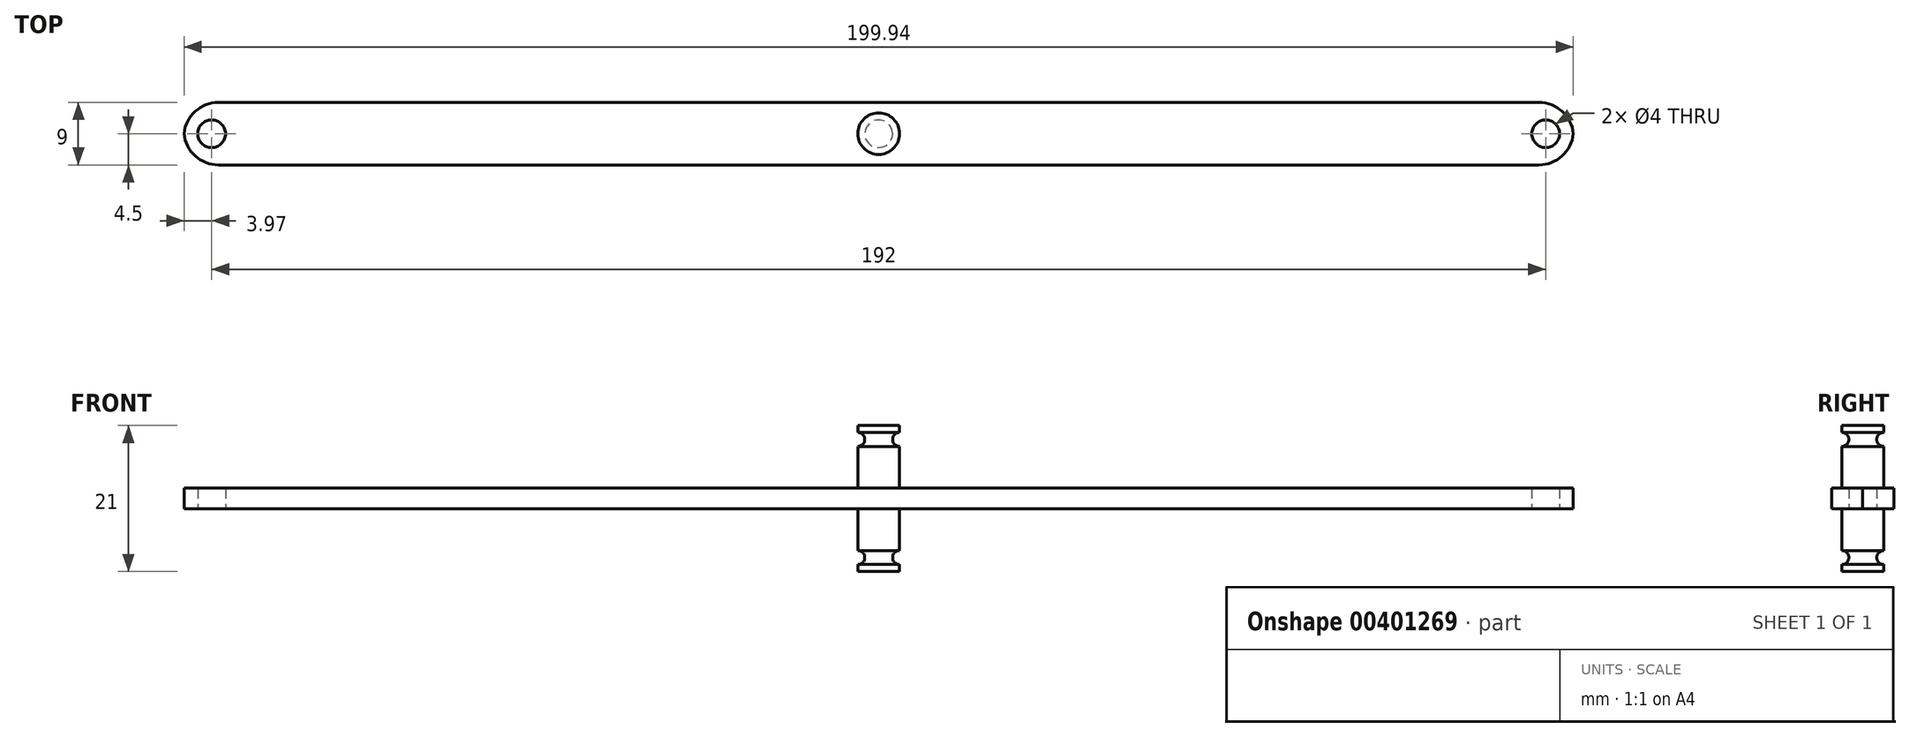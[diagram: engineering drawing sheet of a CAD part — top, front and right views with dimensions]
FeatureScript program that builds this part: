
annotation { "Feature Type Name" : "Feature", "Feature Type Description" : "" }
export const myFeature = defineFeature(function(context is Context, id is Id, definition is map)
    precondition{}
    {
        {
            var Q0;
            Q0=qCreatedBy(makeId("Top.planeOp"),FACE);
            var sketch = newSketch(context, id + "F0", { "sketchPlane" : qUnion([Q0])});
            skLineSegment(sketch, "E0.bottom", {"start": v(-100, 4.5) * mm, "end": v(100, 4.5) * mm});
            skLineSegment(sketch, "E0.top", {"start": v(-100, -4.5) * mm, "end": v(100, -4.5) * mm});
            skLineSegment(sketch, "E0.left", {"start": v(-100, 4.5) * mm, "end": v(-100, -4.5) * mm});
            skLineSegment(sketch, "E0.right", {"start": v(100, 4.5) * mm, "end": v(100, -4.5) * mm});
            skPoint(sketch, "E0.middle", {"position": v(0, 0) * mm});
            skSolve(sketch);
        }
        {
            var Q0;
            Q0 = qSketchRegion(id + "F0", true);
            extrude(context, id + "F1", {"entities" : qUnion([Q0]), "depth" : 3 * mm});
        }
        {
            var Q0;
            Q0=makeQuery(id+"F1.opExtrude","CAP_FACE",FACE,{"disambiguationData":[OSD([sQuery(id+"F0.wireOp",EDGE,"E0.bottom"),sQuery(id+"F0.wireOp",EDGE,"E0.top"),sQuery(id+"F0.wireOp",EDGE,"E0.left"),sQuery(id+"F0.wireOp",EDGE,"E0.right")])],"isStart":true});
            var sketch = newSketch(context, id + "F2", { "sketchPlane" : qUnion([Q0])});
            skCircle(sketch, "E1", {"center": v(-96, 0) * mm, "radius": 2 * mm});
            skCircle(sketch, "E2.MirrorC", {"center": v(96, 0) * mm, "radius": 2 * mm});
            skSolve(sketch);
        }
        {
            var Q0;
            Q0 = qSketchRegion(id + "F2", true);
            extrude(context, id + "F3", {"entities" : qUnion([Q0]), "operationType" : NewBodyOperationType.REMOVE, "oppositeDirection" : true, "depth" : 25 * mm});
        }
        {
            var Q0;
            Q0=makeQuery(id+"F1.opExtrude","SWEPT_EDGE",EDGE,{"disambiguationData":[OSD([sQuery(id+"F0.wireOp",EDGE,"E0.bottom"),sQuery(id+"F0.wireOp",EDGE,"E0.right")])]});
            var Q1;
            Q1=makeQuery(id+"F1.opExtrude","SWEPT_EDGE",EDGE,{"disambiguationData":[OSD([sQuery(id+"F0.wireOp",EDGE,"E0.top"),sQuery(id+"F0.wireOp",EDGE,"E0.right")])]});
            var Q2;
            Q2=makeQuery(id+"F1.opExtrude","SWEPT_EDGE",EDGE,{"disambiguationData":[OSD([sQuery(id+"F0.wireOp",EDGE,"E0.bottom"),sQuery(id+"F0.wireOp",EDGE,"E0.left")])]});
            var Q3;
            Q3=makeQuery(id+"F1.opExtrude","SWEPT_EDGE",EDGE,{"disambiguationData":[OSD([sQuery(id+"F0.wireOp",EDGE,"E0.top"),sQuery(id+"F0.wireOp",EDGE,"E0.left")])]});
            fillet(context, id + "F4", {"entities" : qUnion([Q0, Q1, Q2, Q3]), "radius" : 5 * mm, "tangentPropagation" : true, "allowEdgeOverflow" : false});
        }
        {
            var Q0;
            Q0=makeQuery(id+"F1.opExtrude","CAP_FACE",FACE,{"disambiguationData":[OSD([sQuery(id+"F0.wireOp",EDGE,"E0.bottom"),sQuery(id+"F0.wireOp",EDGE,"E0.top"),sQuery(id+"F0.wireOp",EDGE,"E0.left"),sQuery(id+"F0.wireOp",EDGE,"E0.right")])],"isStart":false});
            var sketch = newSketch(context, id + "F5", { "sketchPlane" : qUnion([Q0])});
            skCircle(sketch, "E3", {"center": v(0, 0) * mm, "radius": 3 * mm});
            skSolve(sketch);
        }
        {
            var Q0;
            Q0 = qSketchRegion(id + "F5", true);
            extrude(context, id + "F6", {"entities" : qUnion([Q0]), "operationType" : NewBodyOperationType.ADD, "depth" : 9 * mm});
        }
        {
            var Q0;
            Q0=makeQuery(id+"F6.opExtrude","CAP_EDGE",EDGE,{"disambiguationData":[OSD([sQuery(id+"F5.wireOp",EDGE,"E3")])],"isStart":false});
            cPlane(context, id + "F7", {"entities" : qUnion([Q0]), "cplaneType" : CPlaneType.LINE_ANGLE, "offset" : 25 * mm, "angle" : 90 * degree, "width" : 150 * mm, "height" : 150 * mm});
        }
        {
            var Q0;
            Q0=qCreatedBy(id+"F7.planeOp",FACE);
            var sketch = newSketch(context, id + "F8", { "sketchPlane" : qUnion([Q0])});
            skCircle(sketch, "E4", {"center": v(-3, 10) * mm, "radius": 1 * mm});
            skSolve(sketch);
        }
        {
            var Q0;
            Q0=makeQuery(id+"F8.imprint","IMPRINT",FACE,{"disambiguationData":[TD([[makeQuery(id+"F8.imprint","IMPRINT",EDGE,{"derivedFrom":sQuery(id+"F8.wireOp",EDGE,"E4")}),1.0]])]});
            var Q1;
            Q1=sQuery(id+"F8.wireOp",EDGE,"E4");
            var Q2;
            Q2=makeQuery(id+"F6.opExtrude","CAP_EDGE",EDGE,{"disambiguationData":[OSD([sQuery(id+"F5.wireOp",EDGE,"E3")])],"isStart":false});
            revolve(context, id + "F9", {"operationType" : NewBodyOperationType.REMOVE, "entities" : qUnion([Q0]), "surfaceEntities" : qUnion([Q1]), "axis" : qUnion([Q2]), "revolveType" : RevolveType.FULL, "oppositeDirection" : true});
        }
        {
            var Q0;
            {var subQ0=sQuery(id+"F0.wireOp",EDGE,"E0.top");Q0=makeQuery(id+"F4.opFillet","BLEND_EDGE",EDGE,{"blendedFrom":[makeQuery(id+"F1.opExtrude","SWEPT_EDGE",EDGE,{"disambiguationData":[OSD([subQ0,sQuery(id+"F0.wireOp",EDGE,"E0.right")])]}),makeQuery(id+"F1.opExtrude","SWEPT_FACE",FACE,{"disambiguationData":[OSD([subQ0])]})],"blendedInto":[makeQuery(id+"F1.opExtrude","SWEPT_FACE",FACE,{"disambiguationData":[OSD([subQ0])]})]});}
            cPoint(context, id + "F10", {"entities" : qUnion([Q0]), "parameter" : 0.5});
        }
        {
            var Q0;
            {var subQ0=sQuery(id+"F0.wireOp",EDGE,"E0.top");Q0=makeQuery(id+"F4.opFillet","BLEND_EDGE",EDGE,{"blendedFrom":[makeQuery(id+"F1.opExtrude","SWEPT_EDGE",EDGE,{"disambiguationData":[OSD([subQ0,sQuery(id+"F0.wireOp",EDGE,"E0.left")])]}),makeQuery(id+"F1.opExtrude","SWEPT_FACE",FACE,{"disambiguationData":[OSD([subQ0])]})],"blendedInto":[makeQuery(id+"F1.opExtrude","SWEPT_FACE",FACE,{"disambiguationData":[OSD([subQ0])]})]});}
            cPoint(context, id + "F11", {"entities" : qUnion([Q0]), "parameter" : 0.5});
        }
        {
            var Q0;
            {var subQ0=sQuery(id+"F0.wireOp",EDGE,"E0.bottom");Q0=makeQuery(id+"F4.opFillet","BLEND_EDGE",EDGE,{"blendedFrom":[makeQuery(id+"F1.opExtrude","SWEPT_EDGE",EDGE,{"disambiguationData":[OSD([subQ0,sQuery(id+"F0.wireOp",EDGE,"E0.right")])]}),makeQuery(id+"F1.opExtrude","SWEPT_FACE",FACE,{"disambiguationData":[OSD([subQ0])]})],"blendedInto":[makeQuery(id+"F1.opExtrude","SWEPT_FACE",FACE,{"disambiguationData":[OSD([subQ0])]})]});}
            cPoint(context, id + "F12", {"entities" : qUnion([Q0]), "parameter" : 0.5});
        }
        {
            var Q0;
            Q0 = qCreatedBy(id + "F10" ,VERTEX);
            var Q1;
            Q1 = qCreatedBy(id + "F11" ,VERTEX);
            var Q2;
            Q2 = qCreatedBy(id + "F12" ,VERTEX);
            cPlane(context, id + "F13", {"entities" : qUnion([Q0, Q1, Q2]), "cplaneType" : CPlaneType.THREE_POINT, "offset" : 0 * mm, "width" : 150 * mm, "height" : 150 * mm});
        }
        {
            var Q0;
            Q0=makeQuery(id+"F1.opExtrude","SWEPT_BODY",BODY,{"disambiguationData":[OSD([sQuery(id+"F0.wireOp",EDGE,"E0.bottom"),sQuery(id+"F0.wireOp",EDGE,"E0.top"),sQuery(id+"F0.wireOp",EDGE,"E0.left"),sQuery(id+"F0.wireOp",EDGE,"E0.right")])]});
            var Q1;
            Q1=qCreatedBy(id+"F13.planeOp",FACE);
            mirror(context, id + "F14", {"operationType" : NewBodyOperationType.ADD, "entities" : qUnion([Q0]), "mirrorPlane" : qUnion([Q1])});
        }
    });
